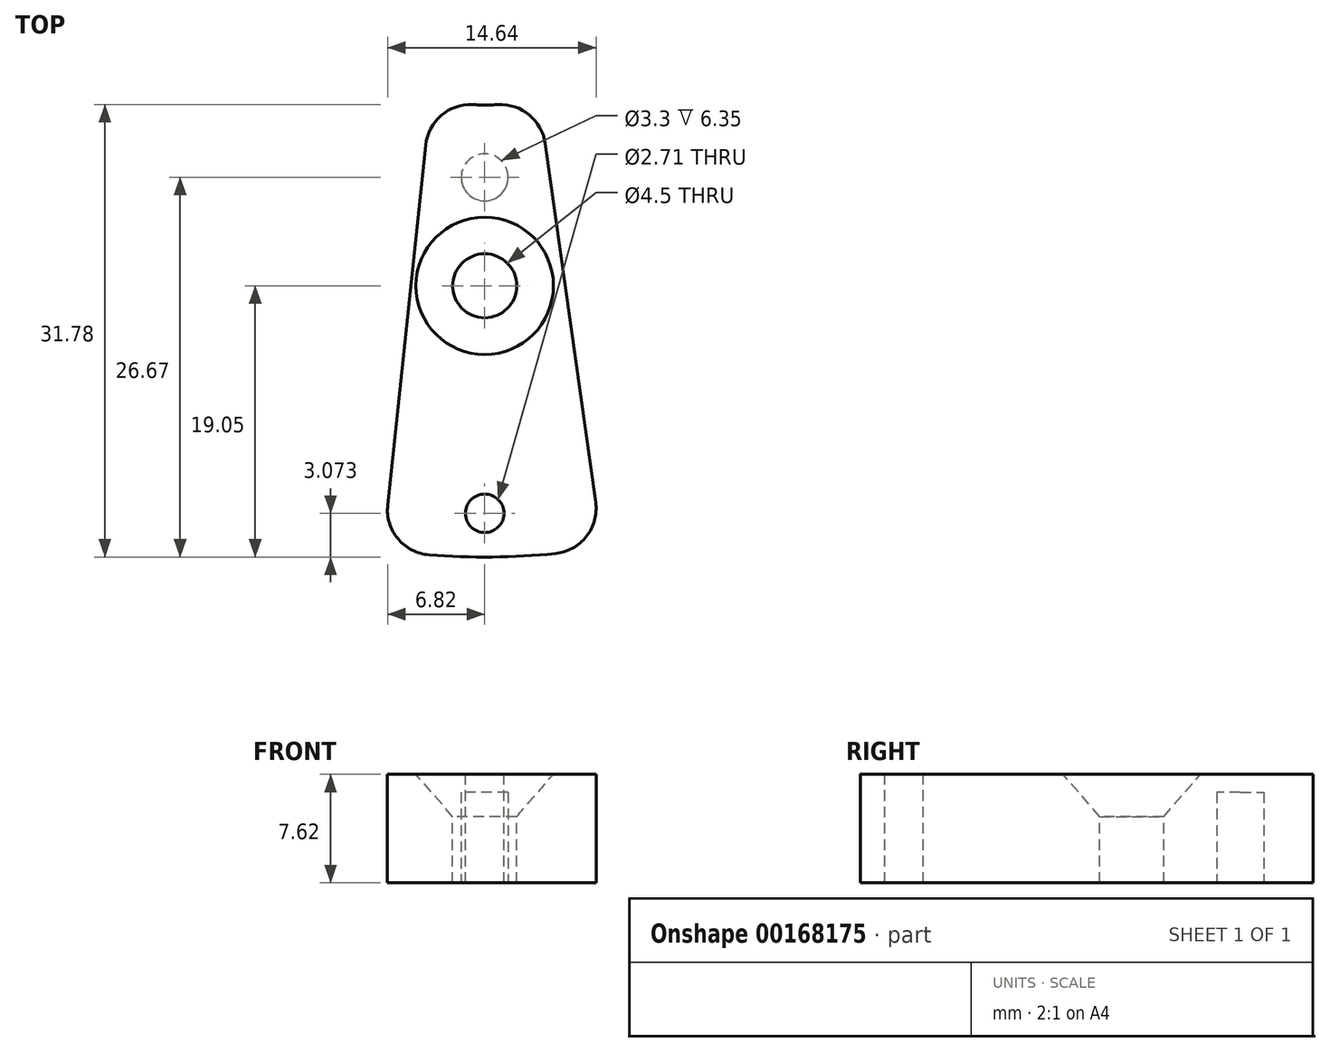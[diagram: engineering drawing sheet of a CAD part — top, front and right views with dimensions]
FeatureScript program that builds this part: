
annotation { "Feature Type Name" : "Feature", "Feature Type Description" : "" }
export const myFeature = defineFeature(function(context is Context, id is Id, definition is map)
    precondition{}
    {
        {
            var Q0;
            Q0=qCreatedBy(makeId("Top.planeOp"),FACE);
            var sketch = newSketch(context, id + "F0", { "sketchPlane" : qUnion([Q0])});
            skArc(sketch, "E0", {"start": v(3.81, -17.37) * mm, "mid": v(0, -17.78) * mm, "end": v(-3.81, -17.37) * mm});
            skArc(sketch, "E1", {"start": v(8.23, -48.84) * mm, "mid": v(0.56, -49.53) * mm, "end": v(-7.14, -49.01) * mm});
            skLineSegment(sketch, "E2", {"start": v(-3.81, -17.37) * mm, "end": v(3.81, -17.37) * mm, "construction": true});
            skLineSegment(sketch, "E3", {"start": v(0, 0) * mm, "end": v(-3.81, -17.37) * mm, "construction": true});
            skLineSegment(sketch, "E4", {"start": v(0, 0) * mm, "end": v(3.81, -17.37) * mm, "construction": true});
            skLineSegment(sketch, "E5", {"start": v(-3.81, -17.37) * mm, "end": v(-7.14, -49.01) * mm});
            skLineSegment(sketch, "E6", {"start": v(3.81, -17.37) * mm, "end": v(8.23, -48.84) * mm});
            skPoint(sketch, "E7", {"position": v(0, -17.37) * mm});
            skSolve(sketch);
        }
        {
            var Q0;
            Q0 = qSketchRegion(id + "F0", true);
            extrude(context, id + "F1", {"entities" : qUnion([Q0]), "depth" : 7.62 * mm});
        }
        {
            var Q0;
            Q0=makeQuery(id+"F1.opExtrude","SWEPT_EDGE",EDGE,{"disambiguationData":[OSD([sQuery(id+"F0.wireOp",EDGE,"E1"),sQuery(id+"F0.wireOp",EDGE,"E5")])]});
            var Q1;
            Q1=makeQuery(id+"F1.opExtrude","SWEPT_EDGE",EDGE,{"disambiguationData":[OSD([sQuery(id+"F0.wireOp",EDGE,"E0"),sQuery(id+"F0.wireOp",EDGE,"E5")])]});
            var Q2;
            Q2=makeQuery(id+"F1.opExtrude","SWEPT_EDGE",EDGE,{"disambiguationData":[OSD([sQuery(id+"F0.wireOp",EDGE,"E1"),sQuery(id+"F0.wireOp",EDGE,"E6")])]});
            var Q3;
            Q3=makeQuery(id+"F1.opExtrude","SWEPT_EDGE",EDGE,{"disambiguationData":[OSD([sQuery(id+"F0.wireOp",EDGE,"E0"),sQuery(id+"F0.wireOp",EDGE,"E6")])]});
            fillet(context, id + "F2", {"entities" : qUnion([Q0, Q1, Q2, Q3]), "radius" : 3.17 * mm, "tangentPropagation" : true, "allowEdgeOverflow" : false});
        }
        {
            var Q0;
            Q0=makeQuery(id+"F1.opExtrude","CAP_FACE",FACE,{"disambiguationData":[OSD([sQuery(id+"F0.wireOp",EDGE,"E0"),sQuery(id+"F0.wireOp",EDGE,"E1"),sQuery(id+"F0.wireOp",EDGE,"E5"),sQuery(id+"F0.wireOp",EDGE,"E6")])],"isStart":false});
            var sketch = newSketch(context, id + "F3", { "sketchPlane" : qUnion([Q0])});
            skPoint(sketch, "E8", {"position": v(0, -46.46) * mm});
            skSolve(sketch);
        }
        {
            var Q0;
            Q0=sQuery(id+"F3.wireOp",VERTEX,"E8");
            var Q1;
            Q1=makeQuery(id+"F1.opExtrude","SWEPT_BODY",BODY,{"disambiguationData":[OSD([sQuery(id+"F0.wireOp",EDGE,"E0"),sQuery(id+"F0.wireOp",EDGE,"E1"),sQuery(id+"F0.wireOp",EDGE,"E5"),sQuery(id+"F0.wireOp",EDGE,"E6")])]});
            hole(context, id + "F4", {"style" : HoleStyle.SIMPLE, "endStyle" : HoleEndStyle.THROUGH, "standardTappedOrClearance" : lookupTablePath({ "standard" : "ANSI", "engagement" : "75%", "pitch" : "32 tpi", "size" : "#6", "type" : "Tapped" }), "standardBlindInLast" : lookupTablePath({ "standard" : "ANSI", "engagement" : "75%", "pitch" : "32 tpi", "size" : "#6", "type" : "Tapped" }), "holeDiameter" : 2.7 * mm, "locations" : qUnion([Q0]), "scope" : qUnion([Q1]), "isTappedThrough" : true, "majorDiameter" : 3.5 * mm, "showTappedDepth" : true});
        }
        {
            var Q0;
            Q0=makeQuery(id+"F1.opExtrude","CAP_FACE",FACE,{"disambiguationData":[OSD([sQuery(id+"F0.wireOp",EDGE,"E0"),sQuery(id+"F0.wireOp",EDGE,"E1"),sQuery(id+"F0.wireOp",EDGE,"E5"),sQuery(id+"F0.wireOp",EDGE,"E6")])],"isStart":false});
            var sketch = newSketch(context, id + "F5", { "sketchPlane" : qUnion([Q0])});
            skPoint(sketch, "E9", {"position": v(0, -30.48) * mm});
            skSolve(sketch);
        }
        {
            var Q0;
            Q0=sQuery(id+"F5.wireOp",VERTEX,"E9");
            var Q1;
            Q1=makeQuery(id+"F1.opExtrude","SWEPT_BODY",BODY,{"disambiguationData":[OSD([sQuery(id+"F0.wireOp",EDGE,"E0"),sQuery(id+"F0.wireOp",EDGE,"E1"),sQuery(id+"F0.wireOp",EDGE,"E5"),sQuery(id+"F0.wireOp",EDGE,"E6")])]});
            hole(context, id + "F6", {"style" : HoleStyle.C_SINK, "endStyle" : HoleEndStyle.THROUGH, "holeDiameter" : 4.5 * mm, "cSinkDiameter" : 9.65 * mm, "cSinkAngle" : 82 * degree, "locations" : qUnion([Q0]), "scope" : qUnion([Q1]), "isTappedThrough" : true});
        }
        {
            var Q0;
            Q0=makeQuery(id+"F1.opExtrude","CAP_FACE",FACE,{"disambiguationData":[OSD([sQuery(id+"F0.wireOp",EDGE,"E0"),sQuery(id+"F0.wireOp",EDGE,"E1"),sQuery(id+"F0.wireOp",EDGE,"E5"),sQuery(id+"F0.wireOp",EDGE,"E6")])],"isStart":true});
            var sketch = newSketch(context, id + "F7", { "sketchPlane" : qUnion([Q0])});
            skCircle(sketch, "E10", {"center": v(0, 22.86) * mm, "radius": 1.65 * mm});
            skSolve(sketch);
        }
        {
            var Q0;
            Q0 = qSketchRegion(id + "F7", true);
            extrude(context, id + "F8", {"entities" : qUnion([Q0]), "operationType" : NewBodyOperationType.REMOVE, "endBound" : BoundingType.THROUGH_ALL, "oppositeDirection" : true, "depth" : 25.4 * mm});
        }
        {
            var Q0;
            Q0=makeQuery(id+"F1.opExtrude","CAP_FACE",FACE,{"disambiguationData":[OSD([sQuery(id+"F0.wireOp",EDGE,"E0"),sQuery(id+"F0.wireOp",EDGE,"E1"),sQuery(id+"F0.wireOp",EDGE,"E5"),sQuery(id+"F0.wireOp",EDGE,"E6")])],"isStart":false});
            var sketch = newSketch(context, id + "F9", { "sketchPlane" : qUnion([Q0])});
            skCircle(sketch, "E11.0", {"center": v(0, -22.86) * mm, "radius": 1.65 * mm});
            skSolve(sketch);
        }
        {
            var Q0;
            Q0 = qSketchRegion(id + "F9", true);
            extrude(context, id + "F10", {"entities" : qUnion([Q0]), "operationType" : NewBodyOperationType.ADD, "oppositeDirection" : true, "depth" : 1.27 * mm});
        }
    });
